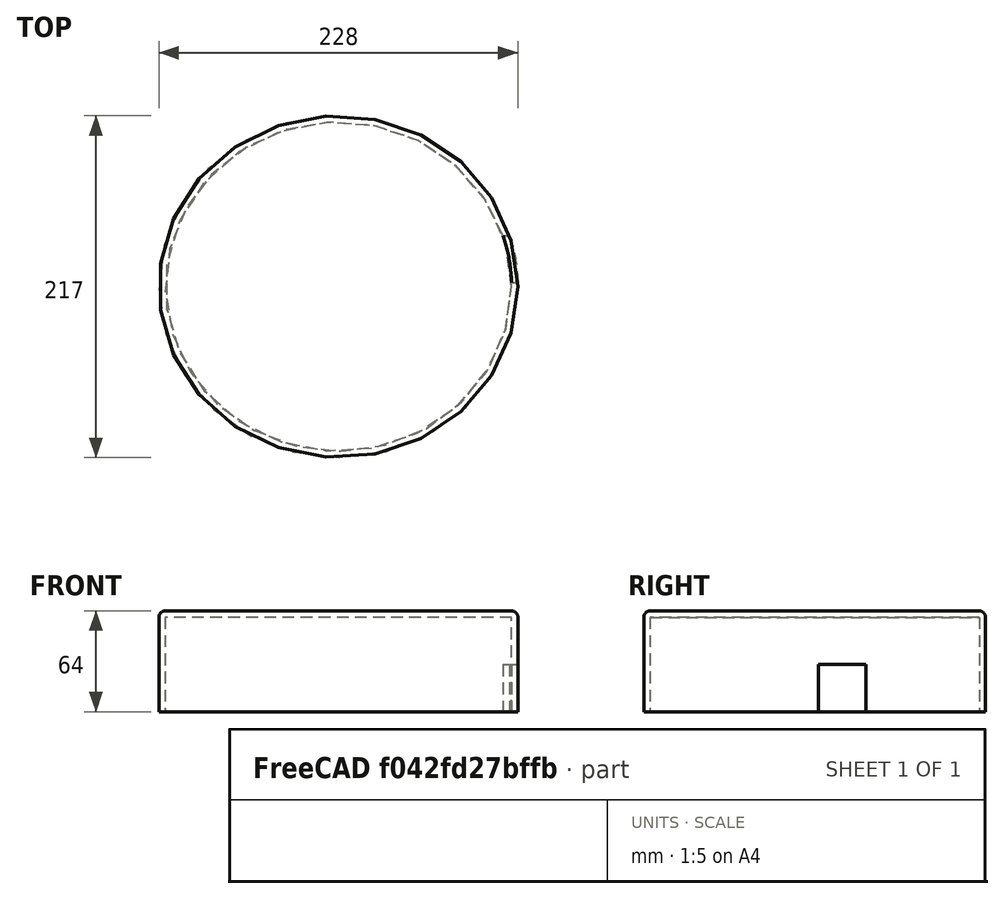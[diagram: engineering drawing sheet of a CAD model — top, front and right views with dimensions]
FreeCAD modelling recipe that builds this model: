
FCSTD DOCUMENT  (FreeCAD 0.14R2935 (Git))
Label: Base_monitor_LG_W2242S
License: CC-BY 3.0
LicenseURL: http://creativecommons.org/licenses/by/3.0/
objects: Part::Part2DObjectPython×1, Part::Extrusion×1, Part::Thickness×1, Part::Box×1, Part::Cut×1
note: 5 computed .brp shape members not serialized (recipe doc carries the construction recipe); baked Part::Feature solids carry a one-line shape summary decoded from their .brp

FEATURE [Part::Part2DObjectPython] Ellipse  # Draft 2D object (typed FeaturePython)
  MajorRadius = 110
  MinorRadius = 104.5
  Placement = pos=(3.5,-2.5,0) rot=(0,0,1;0rad)
FEATURE [Part::Extrusion] Extrude
  Base = -> Ellipse
  Dir = (0,0,60)
  Solid = true
FEATURE [Part::Thickness] Thickness  label="Base"
  Faces = -> Extrude [Face2]
  Intersection = false
  Join = 0
  Mode = 0
  SelfIntersection = false
  Value = 4
FEATURE [Part::Box] Box
  Height = 30
  Length = 25
  Placement = pos=(104,0,0) rot=(0,0,1;0rad)
  Width = 30
FEATURE [Part::Cut] Cut
  Base = -> Thickness
  Tool = -> Box
